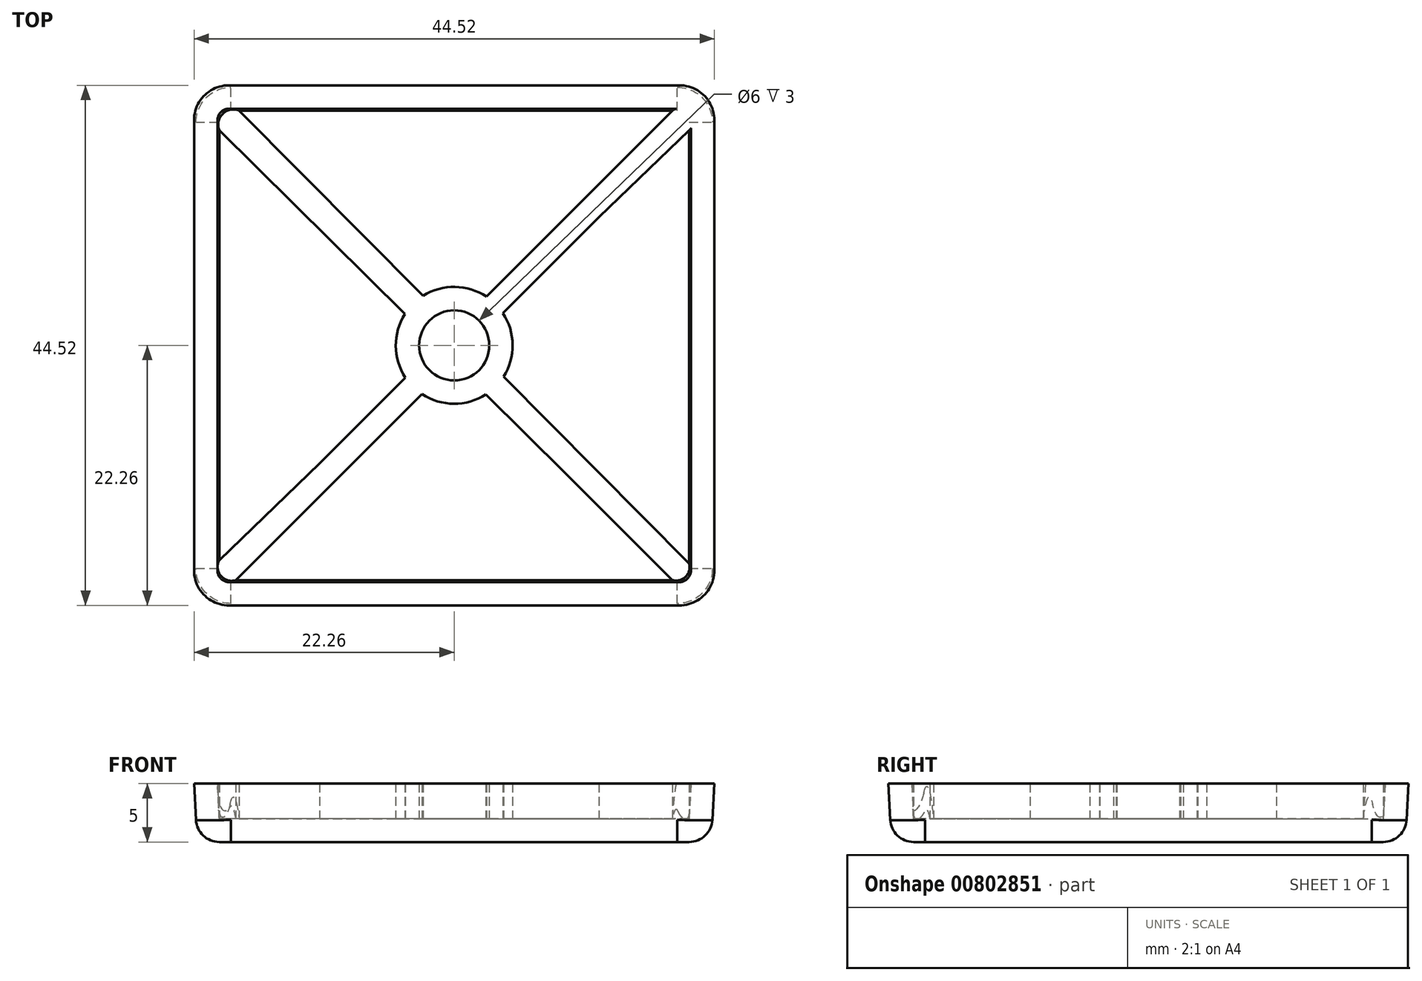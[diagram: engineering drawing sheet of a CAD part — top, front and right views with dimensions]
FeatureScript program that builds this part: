
annotation { "Feature Type Name" : "Feature", "Feature Type Description" : "" }
export const myFeature = defineFeature(function(context is Context, id is Id, definition is map)
    precondition{}
    {
        {
            var Q0;
            Q0=qCreatedBy(makeId("Top.planeOp"),FACE);
            var sketch = newSketch(context, id + "F0", { "sketchPlane" : qUnion([Q0])});
            skLineSegment(sketch, "E0.bottom", {"start": v(0, 0) * mm, "end": v(44, 0) * mm});
            skLineSegment(sketch, "E0.top", {"start": v(0, 44) * mm, "end": v(44, 44) * mm});
            skLineSegment(sketch, "E0.left", {"start": v(0, 0) * mm, "end": v(0, 44) * mm});
            skLineSegment(sketch, "E0.right", {"start": v(44, 0) * mm, "end": v(44, 44) * mm});
            skSolve(sketch);
        }
        {
            var Q0;
            Q0 = qSketchRegion(id + "F0", true);
            extrude(context, id + "F1", {"entities" : qUnion([Q0]), "depth" : 5 * mm, "offsetDistance" : 25 * mm, "hasDraft" : true, "draftAngle" : 3 * degree});
        }
        {
            var Q0;
            Q0=makeQuery(id+"F1.opExtrude","SWEPT_EDGE",EDGE,{"disambiguationData":[OSD([sQuery(id+"F0.wireOp",EDGE,"E0.bottom"),sQuery(id+"F0.wireOp",EDGE,"E0.left")])]});
            var Q1;
            Q1=makeQuery(id+"F1.opExtrude","SWEPT_EDGE",EDGE,{"disambiguationData":[OSD([sQuery(id+"F0.wireOp",EDGE,"E0.bottom"),sQuery(id+"F0.wireOp",EDGE,"E0.right")])]});
            var Q2;
            Q2=makeQuery(id+"F1.opExtrude","SWEPT_EDGE",EDGE,{"disambiguationData":[OSD([sQuery(id+"F0.wireOp",EDGE,"E0.top"),sQuery(id+"F0.wireOp",EDGE,"E0.right")])]});
            var Q3;
            Q3=makeQuery(id+"F1.opExtrude","SWEPT_EDGE",EDGE,{"disambiguationData":[OSD([sQuery(id+"F0.wireOp",EDGE,"E0.top"),sQuery(id+"F0.wireOp",EDGE,"E0.left")])]});
            fillet(context, id + "F2", {"entities" : qUnion([Q0, Q1, Q2, Q3]), "radius" : 3 * mm, "tangentPropagation" : true, "allowEdgeOverflow" : false});
        }
        {
            var Q0;
            Q0=makeQuery(id+"F1.opExtrude","CAP_FACE",FACE,{"disambiguationData":[OSD([sQuery(id+"F0.wireOp",EDGE,"E0.bottom"),sQuery(id+"F0.wireOp",EDGE,"E0.top"),sQuery(id+"F0.wireOp",EDGE,"E0.left"),sQuery(id+"F0.wireOp",EDGE,"E0.right")])],"isStart":false});
            shell(context, id + "F3", {"entities" : qUnion([Q0]), "thickness" : 2 * mm});
        }
        {
            var Q0;
            Q0=makeQuery(id+"F3.opShell","OFFSET_FACE",FACE,{"disambiguationData":[OSD([sQuery(id+"F0.wireOp",EDGE,"E0.bottom"),sQuery(id+"F0.wireOp",EDGE,"E0.top"),sQuery(id+"F0.wireOp",EDGE,"E0.left"),sQuery(id+"F0.wireOp",EDGE,"E0.right")])]});
            var sketch = newSketch(context, id + "F4", { "sketchPlane" : qUnion([Q0])});
            skArc(sketch, "E1", {"start": v(26.22, 19.32) * mm, "mid": v(27, 22.04) * mm, "end": v(26.17, 24.76) * mm});
            skCircle(sketch, "E2", {"center": v(22, 22) * mm, "radius": 3 * mm});
            skLineSegment(sketch, "E3", {"start": v(31.54, 11.04) * mm, "end": v(24.72, 17.8) * mm});
            skPoint(sketch, "E3.endSnap0", {"position": v(2.2, 40.4) * mm});
            skLineSegment(sketch, "E4", {"start": v(31.54, 11.04) * mm, "end": v(40.69, 1.9) * mm});
            skLineSegment(sketch, "E5", {"start": v(42.1, 3.31) * mm, "end": v(26.22, 19.32) * mm});
            skPoint(sketch, "E5.endSnap0", {"position": v(3.6, 41.8) * mm});
            skLineSegment(sketch, "E6.trimOffspring", {"start": v(17.78, 24.67) * mm, "end": v(1.9, 40.4) * mm});
            skLineSegment(sketch, "E7.trimOffspring", {"start": v(19.35, 26.24) * mm, "end": v(3.6, 42.1) * mm});
            skArc(sketch, "E8.trimOffspring", {"start": v(17.78, 24.67) * mm, "mid": v(17, 21.95) * mm, "end": v(17.83, 19.24) * mm});
            skLineSegment(sketch, "E9", {"start": v(11.88, 10.47) * mm, "end": v(19.24, 17.83) * mm});
            skLineSegment(sketch, "E10", {"start": v(10.47, 11.88) * mm, "end": v(17.83, 19.24) * mm});
            skLineSegment(sketch, "E11", {"start": v(11.88, 10.47) * mm, "end": v(3.31, 1.9) * mm});
            skLineSegment(sketch, "E12", {"start": v(10.47, 11.88) * mm, "end": v(1.9, 3.6) * mm});
            skPoint(sketch, "E12.endSnap0", {"position": v(2.2, 3.6) * mm});
            skArc(sketch, "E13.trimOffspring", {"start": v(19.24, 17.83) * mm, "mid": v(21.98, 17) * mm, "end": v(24.72, 17.8) * mm});
            skLineSegment(sketch, "E14", {"start": v(34.38, 32.97) * mm, "end": v(26.17, 24.76) * mm});
            skLineSegment(sketch, "E15", {"start": v(32.97, 34.38) * mm, "end": v(24.76, 26.17) * mm});
            skLineSegment(sketch, "E16", {"start": v(34.38, 32.97) * mm, "end": v(42.1, 40.4) * mm});
            skPoint(sketch, "E16.endSnap0", {"position": v(41.8, 40.4) * mm});
            skLineSegment(sketch, "E17", {"start": v(32.97, 34.38) * mm, "end": v(41.1, 42.52) * mm});
            skArc(sketch, "E18.trimOffspring", {"start": v(24.76, 26.17) * mm, "mid": v(22.06, 27) * mm, "end": v(19.35, 26.24) * mm});
            skPoint(sketch, "E19.orphan", {"position": v(25.54, 25.54) * mm});
            skPoint(sketch, "E20.trimOffspring.end.orphan", {"position": v(41.8, 41.8) * mm});
            skPoint(sketch, "E20.trimOffspring.start.orphan", {"position": v(33.67, 33.67) * mm});
            skArc(sketch, "E21", {"start": v(1.9, 3.6) * mm, "mid": v(2.03, 2.27) * mm, "end": v(3.31, 1.9) * mm});
            skArc(sketch, "E22", {"start": v(3.6, 42.1) * mm, "mid": v(2.18, 41.82) * mm, "end": v(1.9, 40.4) * mm});
            skArc(sketch, "E23", {"start": v(40.69, 1.9) * mm, "mid": v(41.8, 2.2) * mm, "end": v(42.1, 3.31) * mm});
            skArc(sketch, "E24", {"start": v(42.1, 40.4) * mm, "mid": v(42.19, 41.9) * mm, "end": v(40.69, 42.1) * mm});
            skSolve(sketch);
        }
        {
            var Q0;
            Q0 = qSketchRegion(id + "F4", true);
            var Q1;
            Q1=makeQuery(id+"F1.opExtrude","CAP_FACE",FACE,{"disambiguationData":[OSD([sQuery(id+"F0.wireOp",EDGE,"E0.bottom"),sQuery(id+"F0.wireOp",EDGE,"E0.top"),sQuery(id+"F0.wireOp",EDGE,"E0.left"),sQuery(id+"F0.wireOp",EDGE,"E0.right")])],"isStart":false});
            extrude(context, id + "F5", {"entities" : qUnion([Q0]), "operationType" : NewBodyOperationType.ADD, "endBound" : BoundingType.UP_TO_SURFACE, "depth" : 25 * mm, "endBoundEntityFace" : qUnion([Q1]), "offsetDistance" : 25 * mm});
        }
        {
            var Q0;
            Q0=makeQuery(id+"F1.opExtrude","CAP_EDGE",EDGE,{"disambiguationData":[OSD([sQuery(id+"F0.wireOp",EDGE,"E0.right")])],"isStart":true});
            fillet(context, id + "F6", {"entities" : qUnion([Q0]), "radius" : 2 * mm, "tangentPropagation" : true, "allowEdgeOverflow" : false});
        }
    });
